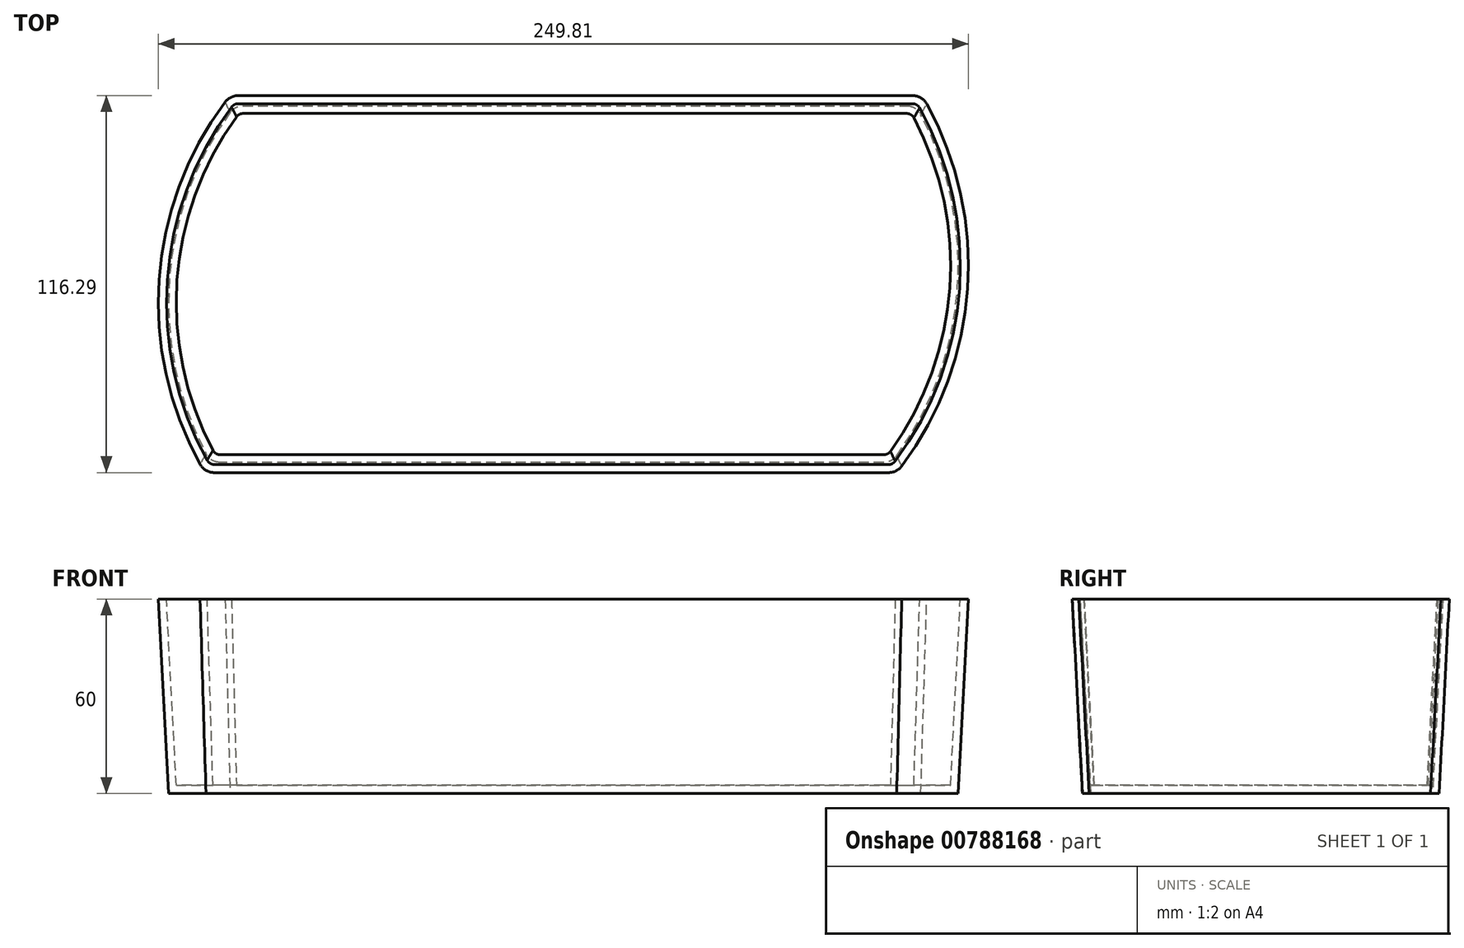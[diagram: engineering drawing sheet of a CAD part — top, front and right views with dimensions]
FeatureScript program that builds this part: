
annotation { "Feature Type Name" : "Feature", "Feature Type Description" : "" }
export const myFeature = defineFeature(function(context is Context, id is Id, definition is map)
    precondition{}
    {
        {
            var Q0;
            Q0=qCreatedBy(makeId("Top.planeOp"),FACE);
            var sketch = newSketch(context, id + "F0", { "sketchPlane" : qUnion([Q0])});
            skLineSegment(sketch, "E0.bottom", {"start": v(-79.48, 60.68) * mm, "end": v(130.52, 60.68) * mm});
            skLineSegment(sketch, "E0.top", {"start": v(-87, -49.32) * mm, "end": v(123, -49.32) * mm});
            skLineSegment(sketch, "E0.left", {"start": v(-79.48, 60.68) * mm, "end": v(-79.48, 60.68) * mm});
            skLineSegment(sketch, "E1", {"start": v(-87, -49.32) * mm, "end": v(-87, -49.32) * mm});
            skArc(sketch, "E2", {"start": v(123, -49.32) * mm, "mid": v(143.3, 4.55) * mm, "end": v(130.52, 60.68) * mm});
            skArc(sketch, "E3", {"start": v(-79.48, 60.68) * mm, "mid": v(-99.77, 6.8) * mm, "end": v(-87, -49.32) * mm});
            skSolve(sketch);
        }
        {
            var Q0;
            Q0=makeQuery(id+"F0.imprint","IMPRINT",FACE,{"disambiguationData":[TD([[makeQuery(id+"F0.imprint","IMPRINT",EDGE,{"derivedFrom":sQuery(id+"F0.wireOp",EDGE,"E0.bottom")}),-1.0]])]});
            extrude(context, id + "F1", {"entities" : qUnion([Q0]), "depth" : 60 * mm, "offsetDistance" : 25 * mm, "hasDraft" : true, "draftAngle" : 3 * degree});
        }
        {
            var Q0;
            Q0=makeQuery(id+"F1.opExtrude","SWEPT_EDGE",EDGE,{"disambiguationData":[OSD([sQuery(id+"F0.wireOp",EDGE,"E0.top"),sQuery(id+"F0.wireOp",EDGE,"E2")])]});
            var Q1;
            Q1=makeQuery(id+"F1.opExtrude","SWEPT_EDGE",EDGE,{"disambiguationData":[OSD([sQuery(id+"F0.wireOp",EDGE,"E0.top"),sQuery(id+"F0.wireOp",EDGE,"E3")])]});
            var Q2;
            Q2=makeQuery(id+"F1.opExtrude","SWEPT_EDGE",EDGE,{"disambiguationData":[OSD([sQuery(id+"F0.wireOp",EDGE,"E0.bottom"),sQuery(id+"F0.wireOp",EDGE,"E3")])]});
            var Q3;
            Q3=makeQuery(id+"F1.opExtrude","SWEPT_EDGE",EDGE,{"disambiguationData":[OSD([sQuery(id+"F0.wireOp",EDGE,"E0.bottom"),sQuery(id+"F0.wireOp",EDGE,"E2")])]});
            fillet(context, id + "F2", {"entities" : qUnion([Q0, Q1, Q2, Q3]), "radius" : 5 * mm, "tangentPropagation" : true, "allowEdgeOverflow" : false});
        }
        {
            var Q0;
            Q0=makeQuery(id+"F1.opExtrude","CAP_FACE",FACE,{"disambiguationData":[OSD([sQuery(id+"F0.wireOp",EDGE,"E0.bottom"),sQuery(id+"F0.wireOp",EDGE,"E0.top"),sQuery(id+"F0.wireOp",EDGE,"E2"),sQuery(id+"F0.wireOp",EDGE,"E3")])],"isStart":false});
            shell(context, id + "F3", {"entities" : qUnion([Q0]), "thickness" : 2.5 * mm});
        }
    });
